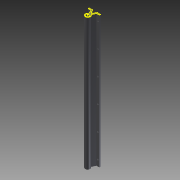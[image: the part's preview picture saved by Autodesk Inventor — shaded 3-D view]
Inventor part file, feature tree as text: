
AUTODESK INVENTOR PART (.ipt)
format: ipt  version: 2013 (Build 170138000, 138)  size: 132,608 bytes
history: native  units: in
note: dims shown in document units (in); Inventor stores cm internally (conversion verified against a paired STEP export)
features: sketch x1, imported_body x1
ambient origin geometry x8: Origin, YZ Plane, XZ Plane, XY Plane, X Axis, Y Axis, Z Axis, Center Point
feature tree (2):
  sketch  "Sketch1"
  imported_body  "Base1"
